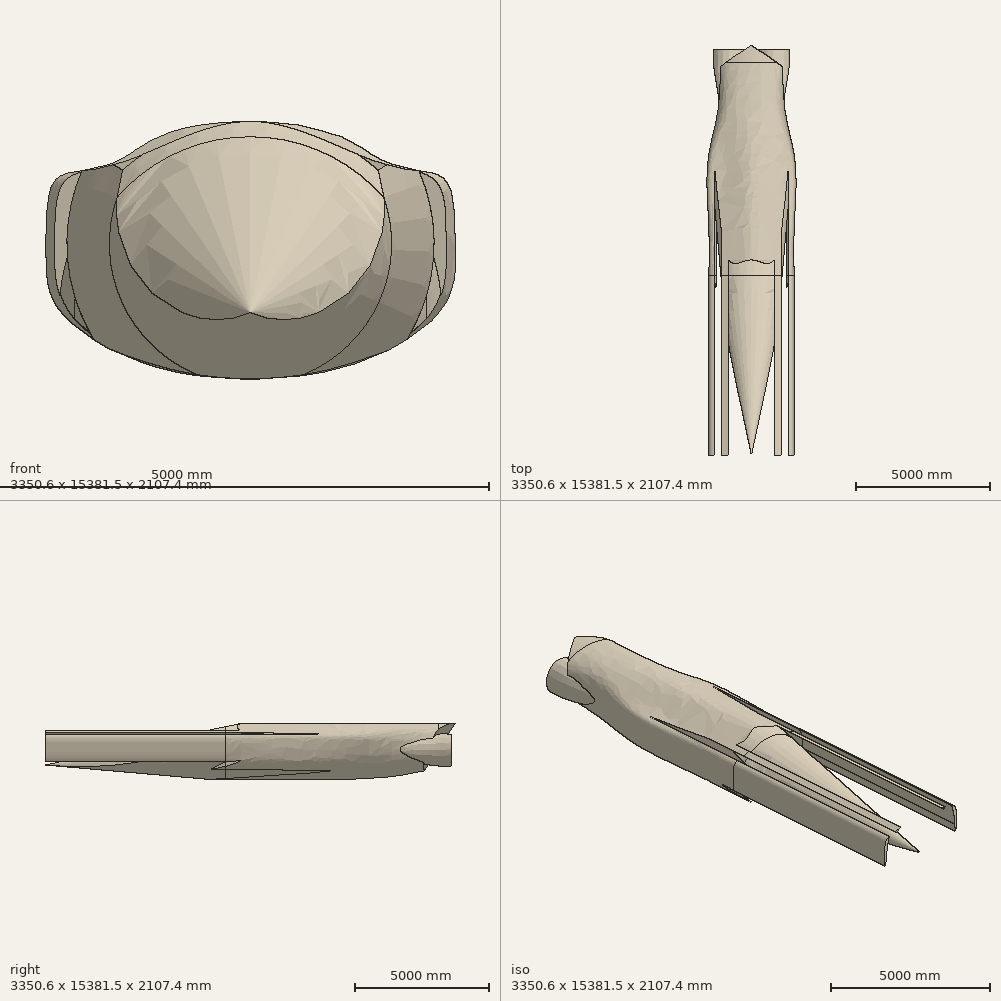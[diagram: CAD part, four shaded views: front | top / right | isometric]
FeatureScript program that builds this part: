
annotation { "Feature Type Name" : "Feature", "Feature Type Description" : "" }
export const myFeature = defineFeature(function(context is Context, id is Id, definition is map)
    precondition{}
    {
        {
            var Q0;
            Q0=qCreatedBy(makeId("Front.planeOp"),FACE);
            cPlane(context, id + "F0", {"entities" : qUnion([Q0]), "cplaneType" : CPlaneType.OFFSET, "offset" : 1750 * mm, "width" : 152.4 * mm, "height" : 152.4 * mm});
        }
        {
            var Q0;
            Q0=qCreatedBy(id+"F0.planeOp",FACE);
            var sketch = newSketch(context, id + "F1", { "sketchPlane" : qUnion([Q0])});
            skPoint(sketch, "E0.middle", {"position": v(0, 0) * mm});
            skFitSpline(sketch, "E1", {"points": [v(0, 1000) * mm, v(1060, 662.5) * mm, v(1517.6, 506.84) * mm, v(1600, 0) * mm, v(1517.6, -506.84) * mm, v(750, -1000) * mm, v(-750, -1000) * mm, v(-1517.6, -506.84) * mm, v(-1600, 0) * mm, v(-1517.6, 506.84) * mm, v(-1060, 662.5) * mm, v(0, 1000) * mm]});
            skSolve(sketch);
        }
        {
            var Q0;
            Q0=qCreatedBy(makeId("Front.planeOp"),FACE);
            var sketch = newSketch(context, id + "F2", { "sketchPlane" : qUnion([Q0])});
            skPoint(sketch, "E2.middle", {"position": v(0, 0) * mm});
            skFitSpline(sketch, "E3", {"points": [v(0, 1000) * mm, v(1060, 662.5) * mm, v(1517.6, 506.84) * mm, v(1600, 0) * mm, v(1517.6, -506.84) * mm, v(750, -1000) * mm, v(-750, -1000) * mm, v(-1517.6, -506.84) * mm, v(-1600, 0) * mm, v(-1517.6, 506.84) * mm, v(-1060, 662.5) * mm, v(0, 1000) * mm]});
            skSolve(sketch);
        }
        {
            var Q0;
            Q0=qCreatedBy(makeId("Front.planeOp"),FACE);
            cPlane(context, id + "F3", {"entities" : qUnion([Q0]), "cplaneType" : CPlaneType.OFFSET, "offset" : 2800 * mm, "oppositeDirection" : true, "width" : 150 * mm, "height" : 150 * mm});
        }
        {
            var Q0;
            Q0=qCreatedBy(id+"F3.planeOp",FACE);
            var sketch = newSketch(context, id + "F4", { "sketchPlane" : qUnion([Q0])});
            skPoint(sketch, "E4.middle", {"position": v(0, 0) * mm});
            skFitSpline(sketch, "E5", {"points": [v(0, 1000) * mm, v(1060, 662.5) * mm, v(1517.6, 506.84) * mm, v(1600, 0) * mm, v(1517.6, -506.84) * mm, v(750, -1000) * mm, v(-750, -1000) * mm, v(-1517.6, -506.84) * mm, v(-1600, 0) * mm, v(-1517.6, 506.84) * mm, v(-1060, 662.5) * mm, v(0, 1000) * mm]});
            skSolve(sketch);
        }
        {
            var Q0;
            Q0=qCreatedBy(makeId("Front.planeOp"),FACE);
            cPlane(context, id + "F5", {"entities" : qUnion([Q0]), "cplaneType" : CPlaneType.OFFSET, "offset" : 4500 * mm, "oppositeDirection" : true, "width" : 150 * mm, "height" : 150 * mm});
        }
        {
            var Q0;
            Q0=qCreatedBy(id+"F5.planeOp",FACE);
            var sketch = newSketch(context, id + "F6", { "sketchPlane" : qUnion([Q0])});
            skPoint(sketch, "E6.middle", {"position": v(0, 0) * mm});
            skFitSpline(sketch, "E7", {"points": [v(0, 1000) * mm, v(1060, 662.5) * mm, v(1250, 0) * mm, v(1060, -662.5) * mm, v(0, -1000) * mm, v(-1060, -662.5) * mm, v(-1250, 0) * mm, v(-1060, 662.5) * mm, v(0, 1000) * mm]});
            skSolve(sketch);
        }
        {
            var Q0;
            Q0=qCreatedBy(makeId("Front.planeOp"),FACE);
            cPlane(context, id + "F7", {"entities" : qUnion([Q0]), "cplaneType" : CPlaneType.OFFSET, "offset" : 6232.05 * mm, "oppositeDirection" : true, "width" : 150 * mm, "height" : 150 * mm});
        }
        {
            var Q0;
            Q0=qCreatedBy(id+"F7.planeOp",FACE);
            var sketch = newSketch(context, id + "F8", { "sketchPlane" : qUnion([Q0])});
            skPoint(sketch, "E8.middle", {"position": v(0, 0) * mm});
            skFitSpline(sketch, "E9", {"points": [v(0, 1000) * mm, v(1060, 662.5) * mm, v(1250, 0) * mm, v(848, -530) * mm, v(-848, -530) * mm, v(-1250, 0) * mm, v(-1060, 662.5) * mm, v(0, 1000) * mm]});
            skSolve(sketch);
        }
        {
            var Q0;
            Q0=qSketchRegion(id+"F1",true);
            var Q1;
            Q1=qSketchRegion(id+"F2",true);
            var Q2;
            Q2=qSketchRegion(id+"F4",true);
            var Q3;
            Q3=qSketchRegion(id+"F6",true);
            var Q4;
            Q4=qSketchRegion(id+"F8",true);
            loft(context, id + "F9", {"sheetProfilesArray" : [{ "sheetProfileEntities" : qUnion([Q0]) }, { "sheetProfileEntities" : qUnion([Q1]) }, { "sheetProfileEntities" : qUnion([Q2]) }, { "sheetProfileEntities" : qUnion([Q3]) }, { "sheetProfileEntities" : qUnion([Q4]) }]});
        }
        {
            var Q0;
            Q0=makeQuery(id+"F9.opLoft","CAP_FACE",FACE,{"disambiguationData":[OSD([makeQuery(id+"F8.imprint","IMPRINT",FACE,{"disambiguationData":[TD([[makeQuery(id+"F8.imprint","IMPRINT",EDGE,{"derivedFrom":sQuery(id+"F8.wireOp",EDGE,"E9")}),-1.0]])]})])],"isStart":true});
            extrude(context, id + "F10", {"entities" : qUnion([Q0]), "operationType" : NewBodyOperationType.ADD, "depth" : 649.4 * mm});
        }
        {
            var Q0;
            Q0=qCreatedBy(makeId("Right.planeOp"),FACE);
            var sketch = newSketch(context, id + "F11", { "sketchPlane" : qUnion([Q0])});
            skLineSegment(sketch, "E10", {"start": v(0, 0) * mm, "end": v(4500, 0) * mm});
            skLineSegment(sketch, "E11", {"start": v(4500, 0) * mm, "end": v(6232.05, 0) * mm});
            skLineSegment(sketch, "E12", {"start": v(4500, 0) * mm, "end": v(4500, 1000) * mm});
            skLineSegment(sketch, "E13", {"start": v(4500, 1000) * mm, "end": v(6881.46, 1000) * mm});
            skLineSegment(sketch, "E14", {"start": v(6881.46, 1000) * mm, "end": v(6881.46, -1000) * mm});
            skLineSegment(sketch, "E15", {"start": v(6232.05, 0) * mm, "end": v(6881.46, 1000) * mm});
            skLineSegment(sketch, "E16", {"start": v(6232.05, 0) * mm, "end": v(5582.64, -1000) * mm});
            skLineSegment(sketch, "E17", {"start": v(5582.64, -1000) * mm, "end": v(6881.46, -1000) * mm});
            skSolve(sketch);
        }
        {
            var Q0;
            Q0=makeQuery(id+"F11.imprint","IMPRINT",FACE,{"disambiguationData":[TD([[makeQuery(id+"F11.imprint","IMPRINT",EDGE,{"derivedFrom":sQuery(id+"F11.wireOp",EDGE,"E14")}),-1.0]])]});
            var Q1;
            Q1=sQuery(id+"F11.wireOp",EDGE,"E13");
            revolve(context, id + "F12", {"operationType" : NewBodyOperationType.REMOVE, "entities" : qUnion([Q0]), "axis" : qUnion([Q1]), "revolveType" : RevolveType.SYMMETRIC, "oppositeDirection" : true, "angle" : 182 * degree});
        }
        {
            var Q0;
            Q0=makeQuery(id+"F9.opLoft","CAP_FACE",FACE,{"disambiguationData":[OSD([makeQuery(id+"F1.imprint","IMPRINT",FACE,{"disambiguationData":[TD([[makeQuery(id+"F1.imprint","IMPRINT",EDGE,{"derivedFrom":sQuery(id+"F1.wireOp",EDGE,"E1")}),-1.0]])]})])],"isStart":true});
            extrude(context, id + "F13", {"entities" : qUnion([Q0]), "depth" : 6750 * mm});
        }
        {
            var Q0;
            Q0=qCreatedBy(makeId("Right.planeOp"),FACE);
            var sketch = newSketch(context, id + "F14", { "sketchPlane" : qUnion([Q0])});
            skLineSegment(sketch, "E18", {"start": v(0, 0) * mm, "end": v(-3500, 0) * mm});
            skLineSegment(sketch, "E19", {"start": v(-3500, 0) * mm, "end": v(-3500, -1000) * mm});
            skLineSegment(sketch, "E20", {"start": v(-3500, -1000) * mm, "end": v(-8500, -1000) * mm});
            skLineSegment(sketch, "E21", {"start": v(-8500, -1000) * mm, "end": v(-8500, -562.56) * mm});
            skLineSegment(sketch, "E22", {"start": v(-1164.58, 0) * mm, "end": v(-1164.58, 1000) * mm});
            skLineSegment(sketch, "E23", {"start": v(-1164.58, 1000) * mm, "end": v(-8500, -562.56) * mm});
            skLineSegment(sketch, "E24", {"start": v(-8500, -562.56) * mm, "end": v(-3500, -1000) * mm});
            skLineSegment(sketch, "E25", {"start": v(-1164.58, 1000) * mm, "end": v(-8500, 1000) * mm});
            skLineSegment(sketch, "E26", {"start": v(-8500, 1000) * mm, "end": v(-8500, -562.56) * mm});
            skLineSegment(sketch, "E27", {"start": v(-8500, -1000) * mm, "end": v(-8500, -1500) * mm});
            skLineSegment(sketch, "E28", {"start": v(-3500, -1000) * mm, "end": v(2215.03, -1500) * mm});
            skLineSegment(sketch, "E29", {"start": v(2215.03, -1500) * mm, "end": v(-8500, -1500) * mm});
            skLineSegment(sketch, "E30", {"start": v(-8500, -562.56) * mm, "end": v(-3500, -562.56) * mm});
            skSolve(sketch);
        }
        {
            var Q0;
            Q0=makeQuery(id+"F14.imprint","IMPRINT",FACE,{"disambiguationData":[TD([[makeQuery(id+"F14.imprint","IMPRINT",EDGE,{"derivedFrom":sQuery(id+"F14.wireOp",EDGE,"E23")}),-1.0]])]});
            var Q1;
            Q1=sQuery(id+"F14.wireOp",EDGE,"E30");
            revolve(context, id + "F15", {"operationType" : NewBodyOperationType.REMOVE, "entities" : qUnion([Q0]), "axis" : qUnion([Q1]), "revolveType" : RevolveType.SYMMETRIC, "oppositeDirection" : true, "angle" : 250 * degree});
        }
        {
            var Q0;
            Q0=makeQuery(id+"F14.imprint","IMPRINT",FACE,{"disambiguationData":[TD([[makeQuery(id+"F14.imprint","IMPRINT",EDGE,{"derivedFrom":sQuery(id+"F14.wireOp",EDGE,"E20")}),-1.0]])]});
            var Q1;
            Q1=makeQuery(id+"F14.imprint","IMPRINT",FACE,{"disambiguationData":[TD([[makeQuery(id+"F14.imprint","IMPRINT",EDGE,{"derivedFrom":sQuery(id+"F14.wireOp",EDGE,"E20")}),1.0]])]});
            var Q2;
            Q2=sQuery(id+"F14.wireOp",EDGE,"E18");
            revolve(context, id + "F16", {"operationType" : NewBodyOperationType.REMOVE, "entities" : qUnion([Q0, Q1]), "axis" : qUnion([Q2]), "revolveType" : RevolveType.SYMMETRIC, "oppositeDirection" : true, "angle" : 240 * degree});
        }
        {
            var Q0;
            Q0=qCreatedBy(makeId("Front.planeOp"),FACE);
            cPlane(context, id + "F17", {"entities" : qUnion([Q0]), "cplaneType" : CPlaneType.OFFSET, "offset" : 3500 * mm, "oppositeDirection" : true, "width" : 150 * mm, "height" : 150 * mm});
        }
        {
            var Q0;
            Q0=qCreatedBy(id+"F17.planeOp",FACE);
            var sketch = newSketch(context, id + "F18", { "sketchPlane" : qUnion([Q0])});
            skCircle(sketch, "E31", {"center": v(-825, 0) * mm, "radius": 600 * mm});
            skCircle(sketch, "E32", {"center": v(825, 0) * mm, "radius": 600 * mm});
            skSolve(sketch);
        }
        {
            var Q0;
            Q0=qCreatedBy(makeId("Front.planeOp"),FACE);
            cPlane(context, id + "F19", {"entities" : qUnion([Q0]), "cplaneType" : CPlaneType.OFFSET, "offset" : 4500 * mm, "oppositeDirection" : true, "width" : 150 * mm, "height" : 150 * mm});
        }
        {
            var Q0;
            Q0=qCreatedBy(id+"F19.planeOp",FACE);
            var sketch = newSketch(context, id + "F20", { "sketchPlane" : qUnion([Q0])});
            skCircle(sketch, "E33", {"center": v(-825, 0) * mm, "radius": 400 * mm});
            skCircle(sketch, "E34", {"center": v(825, 0) * mm, "radius": 400 * mm});
            skSolve(sketch);
        }
        {
            var Q0;
            Q0=qCreatedBy(makeId("Front.planeOp"),FACE);
            cPlane(context, id + "F21", {"entities" : qUnion([Q0]), "cplaneType" : CPlaneType.OFFSET, "offset" : 6232.05 * mm, "oppositeDirection" : true, "width" : 150 * mm, "height" : 150 * mm});
        }
        {
            var Q0;
            Q0=qCreatedBy(id+"F21.planeOp",FACE);
            var sketch = newSketch(context, id + "F22", { "sketchPlane" : qUnion([Q0])});
            skCircle(sketch, "E35", {"center": v(-825, 0) * mm, "radius": 600 * mm});
            skCircle(sketch, "E36", {"center": v(825, 0) * mm, "radius": 600 * mm});
            skSolve(sketch);
        }
        {
            var Q0;
            Q0=qCreatedBy(makeId("Front.planeOp"),FACE);
            cPlane(context, id + "F23", {"entities" : qUnion([Q0]), "cplaneType" : CPlaneType.OFFSET, "offset" : 6732.05 * mm, "oppositeDirection" : true, "width" : 150 * mm, "height" : 150 * mm});
        }
        {
            var Q0;
            Q0=qCreatedBy(id+"F23.planeOp",FACE);
            var sketch = newSketch(context, id + "F24", { "sketchPlane" : qUnion([Q0])});
            skCircle(sketch, "E37", {"center": v(-825, 0) * mm, "radius": 600 * mm});
            skCircle(sketch, "E38", {"center": v(825, 0) * mm, "radius": 600 * mm});
            skSolve(sketch);
        }
        {
            var Q0;
            Q0=makeQuery(id+"F18.imprint","IMPRINT",FACE,{"disambiguationData":[TD([[makeQuery(id+"F18.imprint","IMPRINT",EDGE,{"derivedFrom":sQuery(id+"F18.wireOp",EDGE,"E31")}),1.0]])]});
            var Q1;
            Q1=makeQuery(id+"F20.imprint","IMPRINT",FACE,{"disambiguationData":[TD([[makeQuery(id+"F20.imprint","IMPRINT",EDGE,{"derivedFrom":sQuery(id+"F20.wireOp",EDGE,"E33")}),1.0]])]});
            var Q2;
            Q2=makeQuery(id+"F22.imprint","IMPRINT",FACE,{"disambiguationData":[TD([[makeQuery(id+"F22.imprint","IMPRINT",EDGE,{"derivedFrom":sQuery(id+"F22.wireOp",EDGE,"E35")}),1.0]])]});
            var Q3;
            Q3=makeQuery(id+"F24.imprint","IMPRINT",FACE,{"disambiguationData":[TD([[makeQuery(id+"F24.imprint","IMPRINT",EDGE,{"derivedFrom":sQuery(id+"F24.wireOp",EDGE,"E37")}),1.0]])]});
            loft(context, id + "F25", {"sheetProfilesArray" : [{ "sheetProfileEntities" : qUnion([Q0]) }, { "sheetProfileEntities" : qUnion([Q1]) }, { "sheetProfileEntities" : qUnion([Q2]) }, { "sheetProfileEntities" : qUnion([Q3]) }]});
        }
        {
            var Q0;
            Q0=makeQuery(id+"F18.imprint","IMPRINT",FACE,{"disambiguationData":[TD([[makeQuery(id+"F18.imprint","IMPRINT",EDGE,{"derivedFrom":sQuery(id+"F18.wireOp",EDGE,"E32")}),1.0]])]});
            var Q1;
            Q1=makeQuery(id+"F20.imprint","IMPRINT",FACE,{"disambiguationData":[TD([[makeQuery(id+"F20.imprint","IMPRINT",EDGE,{"derivedFrom":sQuery(id+"F20.wireOp",EDGE,"E34")}),1.0]])]});
            var Q2;
            Q2=makeQuery(id+"F22.imprint","IMPRINT",FACE,{"disambiguationData":[TD([[makeQuery(id+"F22.imprint","IMPRINT",EDGE,{"derivedFrom":sQuery(id+"F22.wireOp",EDGE,"E36")}),1.0]])]});
            var Q3;
            Q3=makeQuery(id+"F24.imprint","IMPRINT",FACE,{"disambiguationData":[TD([[makeQuery(id+"F24.imprint","IMPRINT",EDGE,{"derivedFrom":sQuery(id+"F24.wireOp",EDGE,"E38")}),1.0]])]});
            loft(context, id + "F26", {"sheetProfilesArray" : [{ "sheetProfileEntities" : qUnion([Q0]) }, { "sheetProfileEntities" : qUnion([Q1]) }, { "sheetProfileEntities" : qUnion([Q2]) }, { "sheetProfileEntities" : qUnion([Q3]) }]});
        }
    });
